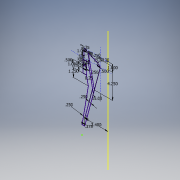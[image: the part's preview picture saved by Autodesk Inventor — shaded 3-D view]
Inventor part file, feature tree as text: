
AUTODESK INVENTOR PART (.ipt)
format: ipt  version: 2017 SP1 (Build 210196100, 196)  size: 128,000 bytes
history: native  units: in
note: dims shown in document units (in); Inventor stores cm internally (conversion verified against a paired STEP export)
features: sketch x1
ambient origin geometry x8: Origin, YZ Plane, XZ Plane, XY Plane, X Axis, Y Axis, Z Axis, Center Point
feature tree (1):
  sketch  "Sketch1"  dims[d0=1.13in d3=0.1718in d5=1.0in d6=1.0in d7=90.0deg d8=0.5in d9=15.0deg d31=0.25in d34=15.0deg d37=1.75in d40=3.75in d41=0.125in d46=0.75in d47=0.5in d51=0.5in d52=0.25in d54=0.5in d55=0.5in d56=1.25in d58=0.0017in d59=0.5in d60=0.5in d61=1.0in d62=0.234in d63=0.234in d64=0.125in d67=0.25in d68=4.25in d69=0.25in d70=0.25in d71=0.375in d73=3.4in d74=1.25in d75=0.2498in]
